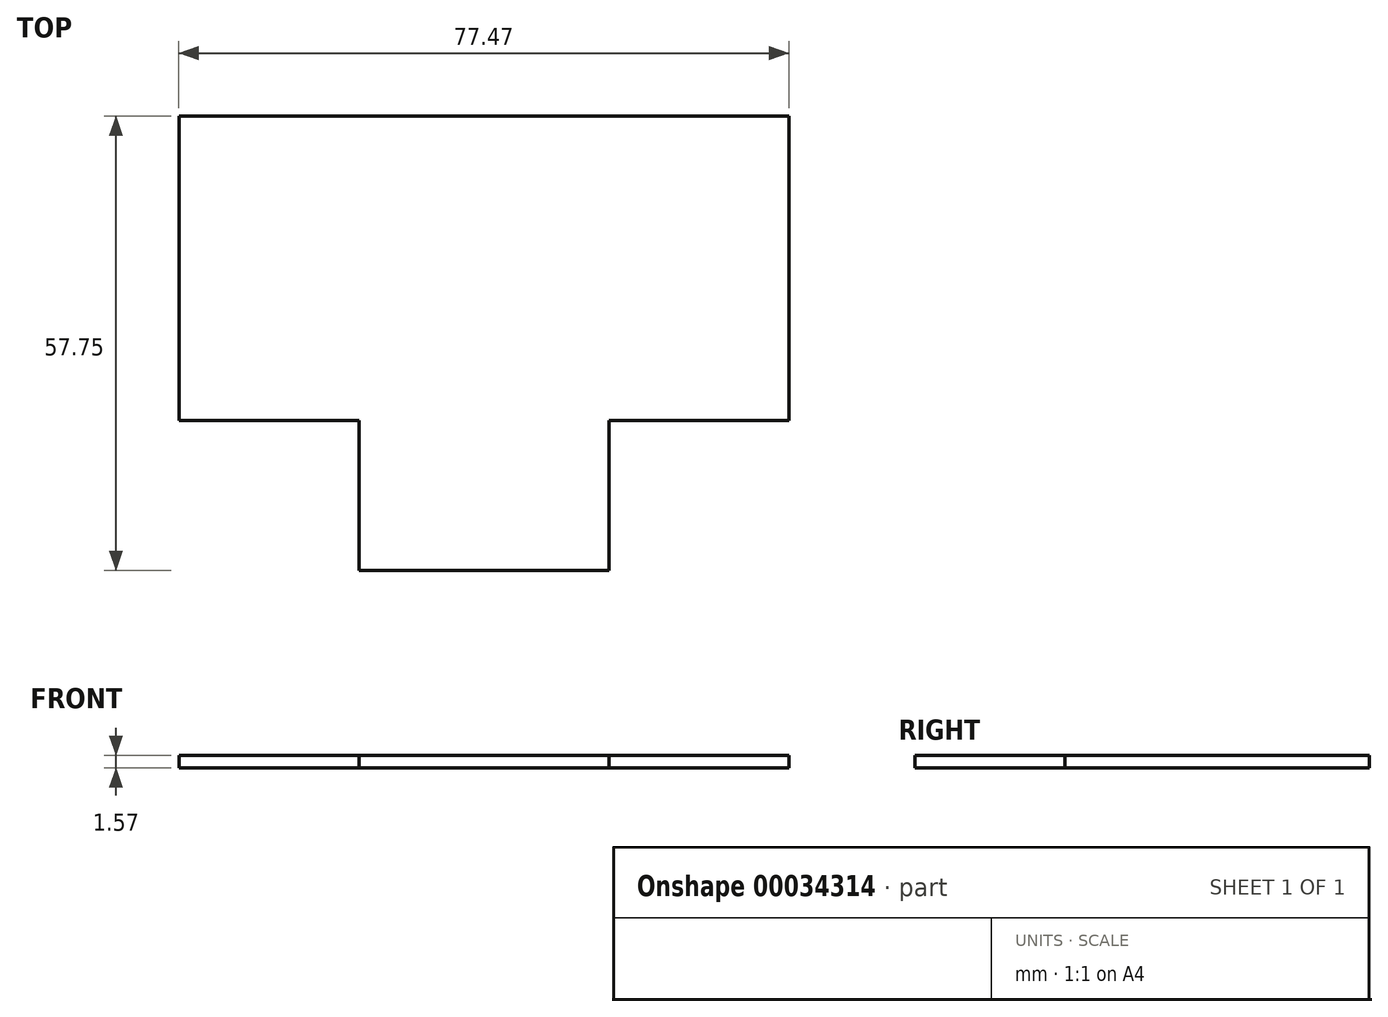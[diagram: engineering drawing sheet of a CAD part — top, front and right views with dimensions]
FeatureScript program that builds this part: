
annotation { "Feature Type Name" : "Feature", "Feature Type Description" : "" }
export const myFeature = defineFeature(function(context is Context, id is Id, definition is map)
    precondition{}
    {
        {
            var Q0;
            Q0=qCreatedBy(makeId("Top.planeOp"),FACE);
            var sketch = newSketch(context, id + "F0", { "sketchPlane" : qUnion([Q0])});
            skLineSegment(sketch, "E0", {"start": v(-27.7, -17.54) * mm, "end": v(-4.84, -17.54) * mm});
            skLineSegment(sketch, "E1", {"start": v(-4.84, -17.54) * mm, "end": v(-4.84, -36.59) * mm});
            skLineSegment(sketch, "E2", {"start": v(-4.84, -36.59) * mm, "end": v(26.91, -36.59) * mm});
            skLineSegment(sketch, "E3", {"start": v(26.91, -36.59) * mm, "end": v(26.91, -17.54) * mm});
            skLineSegment(sketch, "E4", {"start": v(26.91, -17.54) * mm, "end": v(49.77, -17.54) * mm});
            skLineSegment(sketch, "E5", {"start": v(49.77, -17.54) * mm, "end": v(49.77, 21.16) * mm});
            skLineSegment(sketch, "E6", {"start": v(49.77, 21.16) * mm, "end": v(-27.7, 21.16) * mm});
            skLineSegment(sketch, "E7", {"start": v(-27.7, 21.16) * mm, "end": v(-27.7, -17.54) * mm});
            skSolve(sketch);
        }
        {
            var Q0;
            Q0=makeQuery(id+"F0.imprint","IMPRINT",FACE,{"disambiguationData":[TD([[makeQuery(id+"F0.imprint","IMPRINT",EDGE,{"derivedFrom":sQuery(id+"F0.wireOp",EDGE,"E0")}),1.0]])]});
            extrude(context, id + "F1", {"entities" : qUnion([Q0]), "depth" : 1.57 * mm});
        }
    });
